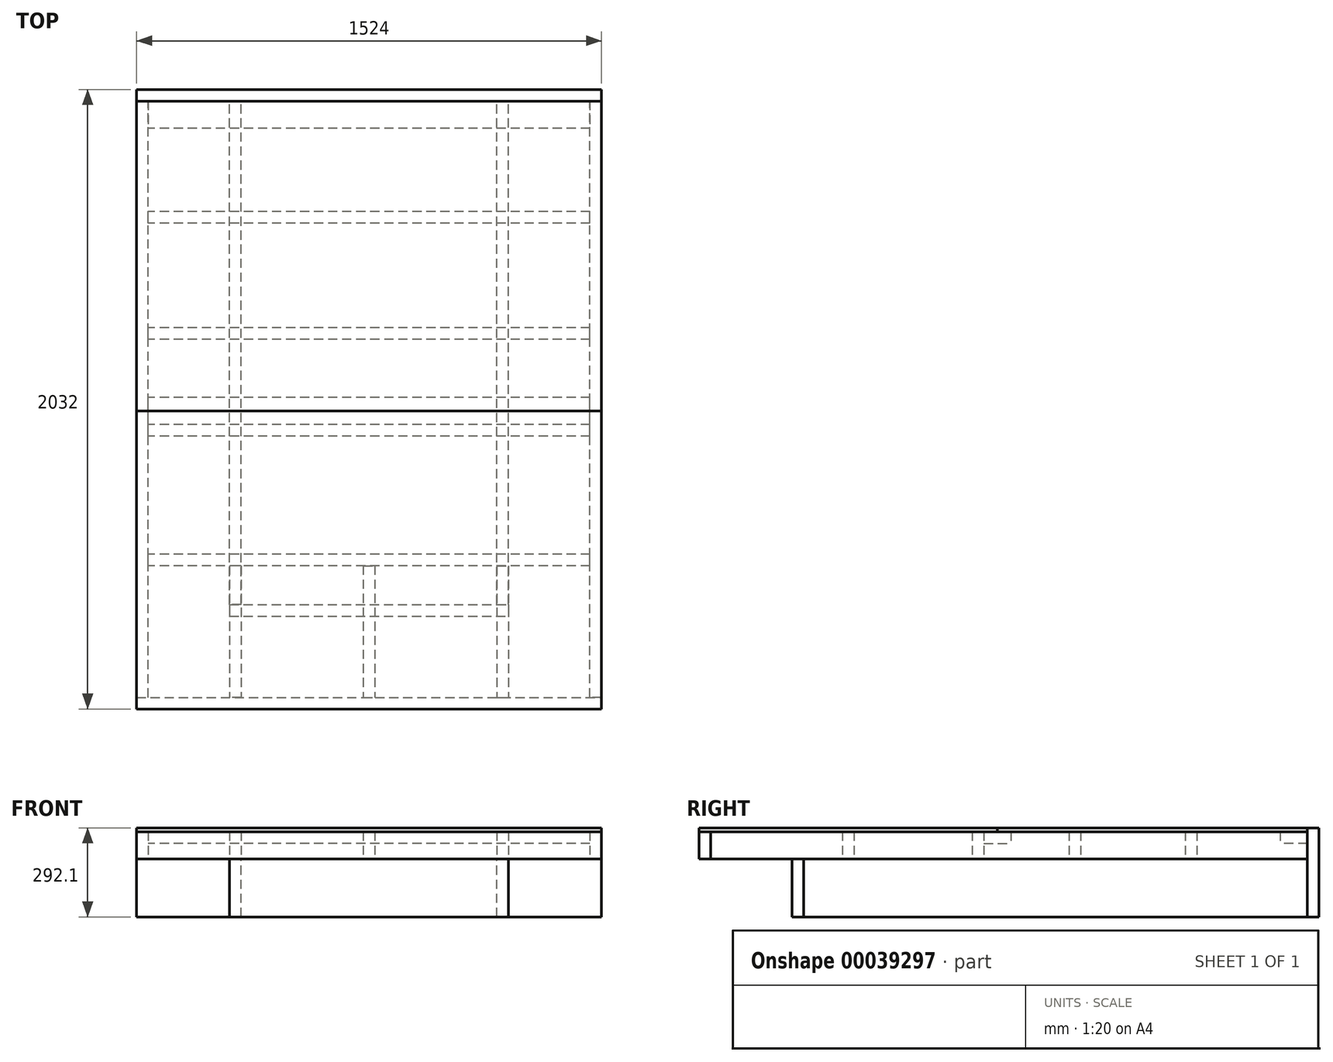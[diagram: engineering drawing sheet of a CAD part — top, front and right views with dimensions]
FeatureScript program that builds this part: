
annotation { "Feature Type Name" : "Feature", "Feature Type Description" : "" }
export const myFeature = defineFeature(function(context is Context, id is Id, definition is map)
    precondition{}
    {
        {
            var Q0;
            Q0=qCreatedBy(makeId("Front.planeOp"),FACE);
            var sketch = newSketch(context, id + "F0", { "sketchPlane" : qUnion([Q0])});
            skLineSegment(sketch, "E0.bottom", {"start": v(-762, 0) * mm, "end": v(762, 0) * mm});
            skLineSegment(sketch, "E0.top", {"start": v(-762, 292.1) * mm, "end": v(762, 292.1) * mm});
            skLineSegment(sketch, "E0.left", {"start": v(-762, 0) * mm, "end": v(-762, 292.1) * mm});
            skLineSegment(sketch, "E0.right", {"start": v(762, 0) * mm, "end": v(762, 292.1) * mm});
            skSolve(sketch);
        }
        {
            var Q0;
            Q0=makeQuery(id+"F0.imprint","IMPRINT",FACE,{"disambiguationData":[TD([[makeQuery(id+"F0.imprint","IMPRINT",EDGE,{"derivedFrom":sQuery(id+"F0.wireOp",EDGE,"E0.bottom")}),1.0]])]});
            extrude(context, id + "F1", {"entities" : qUnion([Q0]), "depth" : 38.1 * mm});
        }
        {
            var Q0;
            Q0=makeQuery(id+"F1.opExtrude","CAP_FACE",FACE,{"disambiguationData":[OSD([sQuery(id+"F0.wireOp",EDGE,"E0.bottom"),sQuery(id+"F0.wireOp",EDGE,"E0.top"),sQuery(id+"F0.wireOp",EDGE,"E0.left"),sQuery(id+"F0.wireOp",EDGE,"E0.right")])],"isStart":false});
            var sketch = newSketch(context, id + "F2", { "sketchPlane" : qUnion([Q0])});
            skLineSegment(sketch, "E1.bottom", {"start": v(419.1, 0) * mm, "end": v(457.2, 0) * mm});
            skLineSegment(sketch, "E1.top", {"start": v(419.1, 190.5) * mm, "end": v(457.2, 190.5) * mm});
            skLineSegment(sketch, "E1.left", {"start": v(419.1, 0) * mm, "end": v(419.1, 190.5) * mm});
            skLineSegment(sketch, "E1.right", {"start": v(457.2, 0) * mm, "end": v(457.2, 190.5) * mm});
            skSolve(sketch);
        }
        {
            var Q0;
            Q0=makeQuery(id+"F2.imprint","IMPRINT",FACE,{"disambiguationData":[TD([[makeQuery(id+"F2.imprint","IMPRINT",EDGE,{"derivedFrom":sQuery(id+"F2.wireOp",EDGE,"E1.bottom")}),1.0]])]});
            extrude(context, id + "F3", {"entities" : qUnion([Q0]), "depth" : 1651 * mm});
        }
        {
            var Q0;
            Q0=makeQuery(id+"F3.opExtrude","SWEPT_BODY",BODY,{"disambiguationData":[OSD([sQuery(id+"F2.wireOp",EDGE,"E1.bottom"),sQuery(id+"F2.wireOp",EDGE,"E1.top"),sQuery(id+"F2.wireOp",EDGE,"E1.left"),sQuery(id+"F2.wireOp",EDGE,"E1.right")])]});
            var Q1;
            Q1=qCreatedBy(makeId("Right.planeOp"),FACE);
            mirror(context, id + "F4", {"entities" : qUnion([Q0]), "mirrorPlane" : qUnion([Q1])});
        }
        {
            var Q0;
            Q0=makeQuery(id+"F3.opExtrude","SWEPT_FACE",FACE,{"disambiguationData":[OSD([sQuery(id+"F2.wireOp",EDGE,"E1.right")])]});
            var sketch = newSketch(context, id + "F5", { "sketchPlane" : qUnion([Q0])});
            skLineSegment(sketch, "E2.bottom", {"start": v(-1689.1, 190.5) * mm, "end": v(-1727.2, 190.5) * mm});
            skLineSegment(sketch, "E2.top", {"start": v(-1689.1, 0) * mm, "end": v(-1727.2, 0) * mm});
            skLineSegment(sketch, "E2.left", {"start": v(-1689.1, 190.5) * mm, "end": v(-1689.1, 0) * mm});
            skLineSegment(sketch, "E2.right", {"start": v(-1727.2, 190.5) * mm, "end": v(-1727.2, 0) * mm});
            skSolve(sketch);
        }
        {
            var Q0;
            Q0=makeQuery(id+"F5.imprint","IMPRINT",FACE,{"disambiguationData":[TD([[makeQuery(id+"F5.imprint","IMPRINT",EDGE,{"derivedFrom":sQuery(id+"F5.wireOp",EDGE,"E2.bottom")}),1.0]])]});
            extrude(context, id + "F6", {"entities" : qUnion([Q0]), "oppositeDirection" : true, "depth" : 914.4 * mm});
        }
        {
            var Q0;
            Q0=makeQuery(id+"F1.opExtrude","CAP_FACE",FACE,{"disambiguationData":[OSD([sQuery(id+"F0.wireOp",EDGE,"E0.bottom"),sQuery(id+"F0.wireOp",EDGE,"E0.top"),sQuery(id+"F0.wireOp",EDGE,"E0.left"),sQuery(id+"F0.wireOp",EDGE,"E0.right")])],"isStart":false});
            var sketch = newSketch(context, id + "F7", { "sketchPlane" : qUnion([Q0])});
            skLineSegment(sketch, "E3.bottom", {"start": v(-762, 279.4) * mm, "end": v(-723.9, 279.4) * mm});
            skLineSegment(sketch, "E3.top", {"start": v(-762, 190.5) * mm, "end": v(-723.9, 190.5) * mm});
            skLineSegment(sketch, "E3.left", {"start": v(-762, 279.4) * mm, "end": v(-762, 190.5) * mm});
            skLineSegment(sketch, "E3.right", {"start": v(-723.9, 279.4) * mm, "end": v(-723.9, 190.5) * mm});
            skSolve(sketch);
        }
        {
            var Q0;
            Q0=makeQuery(id+"F7.imprint","IMPRINT",FACE,{"disambiguationData":[TD([[makeQuery(id+"F7.imprint","IMPRINT",EDGE,{"derivedFrom":sQuery(id+"F7.wireOp",EDGE,"E3.bottom")}),-1.0]])]});
            extrude(context, id + "F8", {"entities" : qUnion([Q0]), "depth" : 1955.8 * mm});
        }
        {
            var Q0;
            Q0=makeQuery(id+"F8.opExtrude","SWEPT_BODY",BODY,{"disambiguationData":[OSD([sQuery(id+"F7.wireOp",EDGE,"E3.bottom"),sQuery(id+"F7.wireOp",EDGE,"E3.top"),sQuery(id+"F7.wireOp",EDGE,"E3.left"),sQuery(id+"F7.wireOp",EDGE,"E3.right")])]});
            var Q1;
            Q1=qCreatedBy(makeId("Right.planeOp"),FACE);
            mirror(context, id + "F9", {"entities" : qUnion([Q0]), "mirrorPlane" : qUnion([Q1])});
        }
        {
            var Q0;
            Q0=makeQuery(id+"F9.opPattern","COPY",FACE,{"derivedFrom":makeQuery(id+"F8.opExtrude","SWEPT_FACE",FACE,{"disambiguationData":[OSD([sQuery(id+"F7.wireOp",EDGE,"E3.left")])]}),"instanceName":"1"});
            var sketch = newSketch(context, id + "F10", { "sketchPlane" : qUnion([Q0])});
            skLineSegment(sketch, "E4.bottom", {"start": v(-1993.9, 279.4) * mm, "end": v(-2032, 279.4) * mm});
            skLineSegment(sketch, "E4.top", {"start": v(-1993.9, 190.5) * mm, "end": v(-2032, 190.5) * mm});
            skLineSegment(sketch, "E4.left", {"start": v(-1993.9, 279.4) * mm, "end": v(-1993.9, 190.5) * mm});
            skLineSegment(sketch, "E4.right", {"start": v(-2032, 279.4) * mm, "end": v(-2032, 190.5) * mm});
            skSolve(sketch);
        }
        {
            var Q0;
            Q0=qSketchRegion(id+"F10",true);
            extrude(context, id + "F11", {"entities" : qUnion([Q0]), "oppositeDirection" : true, "depth" : 1524 * mm});
        }
        {
            var Q0;
            Q0=makeQuery(id+"F11.opExtrude","SWEPT_FACE",FACE,{"disambiguationData":[OSD([sQuery(id+"F10.wireOp",EDGE,"E4.left")])]});
            var sketch = newSketch(context, id + "F12", { "sketchPlane" : qUnion([Q0])});
            skLineSegment(sketch, "E5.bottom", {"start": v(-457.2, 279.4) * mm, "end": v(-419.1, 279.4) * mm});
            skLineSegment(sketch, "E5.top", {"start": v(-457.2, 190.5) * mm, "end": v(-419.1, 190.5) * mm});
            skLineSegment(sketch, "E5.left", {"start": v(-457.2, 279.4) * mm, "end": v(-457.2, 190.5) * mm});
            skLineSegment(sketch, "E5.right", {"start": v(-419.1, 279.4) * mm, "end": v(-419.1, 190.5) * mm});
            skSolve(sketch);
        }
        {
            var Q0;
            Q0=makeQuery(id+"F12.imprint","IMPRINT",FACE,{"disambiguationData":[TD([[makeQuery(id+"F12.imprint","IMPRINT",EDGE,{"derivedFrom":sQuery(id+"F12.wireOp",EDGE,"E5.bottom")}),1.0]])]});
            extrude(context, id + "F13", {"entities" : qUnion([Q0]), "depth" : 431.8 * mm});
        }
        {
            var Q0;
            Q0=makeQuery(id+"F13.opExtrude","SWEPT_BODY",BODY,{"disambiguationData":[OSD([sQuery(id+"F12.wireOp",EDGE,"E5.bottom"),sQuery(id+"F12.wireOp",EDGE,"E5.top"),sQuery(id+"F12.wireOp",EDGE,"E5.left"),sQuery(id+"F12.wireOp",EDGE,"E5.right")])]});
            var Q1;
            Q1=qCreatedBy(makeId("Right.planeOp"),FACE);
            mirror(context, id + "F14", {"entities" : qUnion([Q0]), "mirrorPlane" : qUnion([Q1])});
        }
        {
            var Q0;
            Q0=makeQuery(id+"F11.opExtrude","SWEPT_FACE",FACE,{"disambiguationData":[OSD([sQuery(id+"F10.wireOp",EDGE,"E4.left")])]});
            var sketch = newSketch(context, id + "F15", { "sketchPlane" : qUnion([Q0])});
            skLineSegment(sketch, "E6.bottom", {"start": v(-19.05, 279.4) * mm, "end": v(19.05, 279.4) * mm});
            skLineSegment(sketch, "E6.top", {"start": v(-19.05, 190.5) * mm, "end": v(19.05, 190.5) * mm});
            skLineSegment(sketch, "E6.left", {"start": v(-19.05, 279.4) * mm, "end": v(-19.05, 190.5) * mm});
            skLineSegment(sketch, "E6.right", {"start": v(19.05, 279.4) * mm, "end": v(19.05, 190.5) * mm});
            skSolve(sketch);
        }
        {
            var Q0;
            Q0=makeQuery(id+"F15.imprint","IMPRINT",FACE,{"disambiguationData":[TD([[makeQuery(id+"F15.imprint","IMPRINT",EDGE,{"derivedFrom":sQuery(id+"F15.wireOp",EDGE,"E6.bottom")}),1.0]])]});
            extrude(context, id + "F16", {"entities" : qUnion([Q0]), "depth" : 431.8 * mm});
        }
        {
            var Q0;
            Q0=makeQuery(id+"F8.opExtrude","SWEPT_FACE",FACE,{"disambiguationData":[OSD([sQuery(id+"F7.wireOp",EDGE,"E3.right")])]});
            var sketch = newSketch(context, id + "F17", { "sketchPlane" : qUnion([Q0])});
            skLineSegment(sketch, "E7.bottom", {"start": v(-1524, 279.4) * mm, "end": v(-1562.1, 279.4) * mm});
            skLineSegment(sketch, "E7.top", {"start": v(-1524, 190.5) * mm, "end": v(-1562.1, 190.5) * mm});
            skLineSegment(sketch, "E7.left", {"start": v(-1524, 279.4) * mm, "end": v(-1524, 190.5) * mm});
            skLineSegment(sketch, "E7.right", {"start": v(-1562.1, 279.4) * mm, "end": v(-1562.1, 190.5) * mm});
            skSolve(sketch);
        }
        {
            var Q0;
            Q0=makeQuery(id+"F17.imprint","IMPRINT",FACE,{"disambiguationData":[TD([[makeQuery(id+"F17.imprint","IMPRINT",EDGE,{"derivedFrom":sQuery(id+"F17.wireOp",EDGE,"E7.bottom")}),-1.0]])]});
            extrude(context, id + "F18", {"entities" : qUnion([Q0]), "depth" : 1447.8 * mm});
        }
        {
            var Q0;
            Q0=makeQuery(id+"F8.opExtrude","SWEPT_FACE",FACE,{"disambiguationData":[OSD([sQuery(id+"F7.wireOp",EDGE,"E3.right")])]});
            var sketch = newSketch(context, id + "F19", { "sketchPlane" : qUnion([Q0])});
            skLineSegment(sketch, "E8.bottom", {"start": v(-1098.55, 279.4) * mm, "end": v(-1009.65, 279.4) * mm});
            skLineSegment(sketch, "E8.top", {"start": v(-1098.55, 241.3) * mm, "end": v(-1009.65, 241.3) * mm});
            skLineSegment(sketch, "E8.left", {"start": v(-1098.55, 279.4) * mm, "end": v(-1098.55, 241.3) * mm});
            skLineSegment(sketch, "E8.right", {"start": v(-1009.65, 279.4) * mm, "end": v(-1009.65, 241.3) * mm});
            skSolve(sketch);
        }
        {
            var Q0;
            Q0=makeQuery(id+"F19.imprint","IMPRINT",FACE,{"disambiguationData":[TD([[makeQuery(id+"F19.imprint","IMPRINT",EDGE,{"derivedFrom":sQuery(id+"F19.wireOp",EDGE,"E8.bottom")}),-1.0]])]});
            extrude(context, id + "F20", {"entities" : qUnion([Q0]), "depth" : 1447.8 * mm});
        }
        {
            var Q0;
            Q0=makeQuery(id+"F8.opExtrude","SWEPT_FACE",FACE,{"disambiguationData":[OSD([sQuery(id+"F7.wireOp",EDGE,"E3.right")])]});
            var sketch = newSketch(context, id + "F21", { "sketchPlane" : qUnion([Q0])});
            skLineSegment(sketch, "E9.bottom", {"start": v(-1136.65, 279.4) * mm, "end": v(-1098.55, 279.4) * mm});
            skLineSegment(sketch, "E9.top", {"start": v(-1136.65, 190.5) * mm, "end": v(-1098.55, 190.5) * mm});
            skLineSegment(sketch, "E9.left", {"start": v(-1136.65, 279.4) * mm, "end": v(-1136.65, 190.5) * mm});
            skLineSegment(sketch, "E9.right", {"start": v(-1098.55, 279.4) * mm, "end": v(-1098.55, 190.5) * mm});
            skSolve(sketch);
        }
        {
            var Q0;
            Q0=makeQuery(id+"F21.imprint","IMPRINT",FACE,{"disambiguationData":[TD([[makeQuery(id+"F21.imprint","IMPRINT",EDGE,{"derivedFrom":sQuery(id+"F21.wireOp",EDGE,"E9.bottom")}),-1.0]])]});
            extrude(context, id + "F22", {"entities" : qUnion([Q0]), "depth" : 1447.8 * mm});
        }
        {
            var Q0;
            Q0=makeQuery(id+"F8.opExtrude","SWEPT_FACE",FACE,{"disambiguationData":[OSD([sQuery(id+"F7.wireOp",EDGE,"E3.right")])]});
            var sketch = newSketch(context, id + "F23", { "sketchPlane" : qUnion([Q0])});
            skLineSegment(sketch, "E10.bottom", {"start": v(-38.1, 279.4) * mm, "end": v(-127, 279.4) * mm});
            skLineSegment(sketch, "E10.top", {"start": v(-38.1, 241.3) * mm, "end": v(-127, 241.3) * mm});
            skLineSegment(sketch, "E10.left", {"start": v(-38.1, 279.4) * mm, "end": v(-38.1, 241.3) * mm});
            skLineSegment(sketch, "E10.right", {"start": v(-127, 279.4) * mm, "end": v(-127, 241.3) * mm});
            skSolve(sketch);
        }
        {
            var Q0;
            Q0=makeQuery(id+"F23.imprint","IMPRINT",FACE,{"disambiguationData":[TD([[makeQuery(id+"F23.imprint","IMPRINT",EDGE,{"derivedFrom":sQuery(id+"F23.wireOp",EDGE,"E10.bottom")}),-1.0]])]});
            extrude(context, id + "F24", {"entities" : qUnion([Q0]), "depth" : 1447.8 * mm});
        }
        {
            var Q0;
            Q0=makeQuery(id+"F8.opExtrude","SWEPT_FACE",FACE,{"disambiguationData":[OSD([sQuery(id+"F7.wireOp",EDGE,"E3.right")])]});
            var sketch = newSketch(context, id + "F25", { "sketchPlane" : qUnion([Q0])});
            skLineSegment(sketch, "E11.bottom", {"start": v(-819.15, 279.4) * mm, "end": v(-781.05, 279.4) * mm});
            skLineSegment(sketch, "E11.top", {"start": v(-819.15, 190.5) * mm, "end": v(-781.05, 190.5) * mm});
            skLineSegment(sketch, "E11.left", {"start": v(-819.15, 279.4) * mm, "end": v(-819.15, 190.5) * mm});
            skLineSegment(sketch, "E11.right", {"start": v(-781.05, 279.4) * mm, "end": v(-781.05, 190.5) * mm});
            skSolve(sketch);
        }
        {
            var Q0;
            Q0=makeQuery(id+"F25.imprint","IMPRINT",FACE,{"disambiguationData":[TD([[makeQuery(id+"F25.imprint","IMPRINT",EDGE,{"derivedFrom":sQuery(id+"F25.wireOp",EDGE,"E11.bottom")}),-1.0]])]});
            extrude(context, id + "F26", {"entities" : qUnion([Q0]), "depth" : 1447.8 * mm});
        }
        {
            var Q0;
            Q0=makeQuery(id+"F8.opExtrude","SWEPT_FACE",FACE,{"disambiguationData":[OSD([sQuery(id+"F7.wireOp",EDGE,"E3.right")])]});
            var sketch = newSketch(context, id + "F27", { "sketchPlane" : qUnion([Q0])});
            skLineSegment(sketch, "E12.bottom", {"start": v(-438.15, 279.4) * mm, "end": v(-400.05, 279.4) * mm});
            skLineSegment(sketch, "E12.top", {"start": v(-438.15, 190.5) * mm, "end": v(-400.05, 190.5) * mm});
            skLineSegment(sketch, "E12.left", {"start": v(-438.15, 279.4) * mm, "end": v(-438.15, 190.5) * mm});
            skLineSegment(sketch, "E12.right", {"start": v(-400.05, 279.4) * mm, "end": v(-400.05, 190.5) * mm});
            skSolve(sketch);
        }
        {
            var Q0;
            Q0=qSketchRegion(id+"F27",true);
            extrude(context, id + "F28", {"entities" : qUnion([Q0]), "depth" : 1447.8 * mm});
        }
        {
            var Q0;
            Q0=makeQuery(id+"F11.opExtrude","SWEPT_FACE",FACE,{"disambiguationData":[OSD([sQuery(id+"F10.wireOp",EDGE,"E4.bottom")])]});
            var sketch = newSketch(context, id + "F29", { "sketchPlane" : qUnion([Q0])});
            skLineSegment(sketch, "E13.bottom", {"start": v(-762, -2032) * mm, "end": v(762, -2032) * mm});
            skLineSegment(sketch, "E13.top", {"start": v(-762, -1054.1) * mm, "end": v(762, -1054.1) * mm});
            skLineSegment(sketch, "E13.left", {"start": v(-762, -2032) * mm, "end": v(-762, -1054.1) * mm});
            skLineSegment(sketch, "E13.right", {"start": v(762, -2032) * mm, "end": v(762, -1054.1) * mm});
            skSolve(sketch);
        }
        {
            var Q0;
            Q0=qSketchRegion(id+"F29",true);
            extrude(context, id + "F30", {"entities" : qUnion([Q0]), "depth" : 12.7 * mm});
        }
        {
            var Q0;
            Q0=makeQuery(id+"F8.opExtrude","SWEPT_FACE",FACE,{"disambiguationData":[OSD([sQuery(id+"F7.wireOp",EDGE,"E3.bottom")])]});
            var sketch = newSketch(context, id + "F31", { "sketchPlane" : qUnion([Q0])});
            skLineSegment(sketch, "E14.bottom", {"start": v(-762, -38.1) * mm, "end": v(762, -38.1) * mm});
            skLineSegment(sketch, "E14.top", {"start": v(-762, -1054.1) * mm, "end": v(762, -1054.1) * mm});
            skLineSegment(sketch, "E14.left", {"start": v(-762, -38.1) * mm, "end": v(-762, -1054.1) * mm});
            skLineSegment(sketch, "E14.right", {"start": v(762, -38.1) * mm, "end": v(762, -1054.1) * mm});
            skSolve(sketch);
        }
        {
            var Q0;
            Q0=qSketchRegion(id+"F31",true);
            extrude(context, id + "F32", {"entities" : qUnion([Q0]), "depth" : 12.7 * mm});
        }
    });
